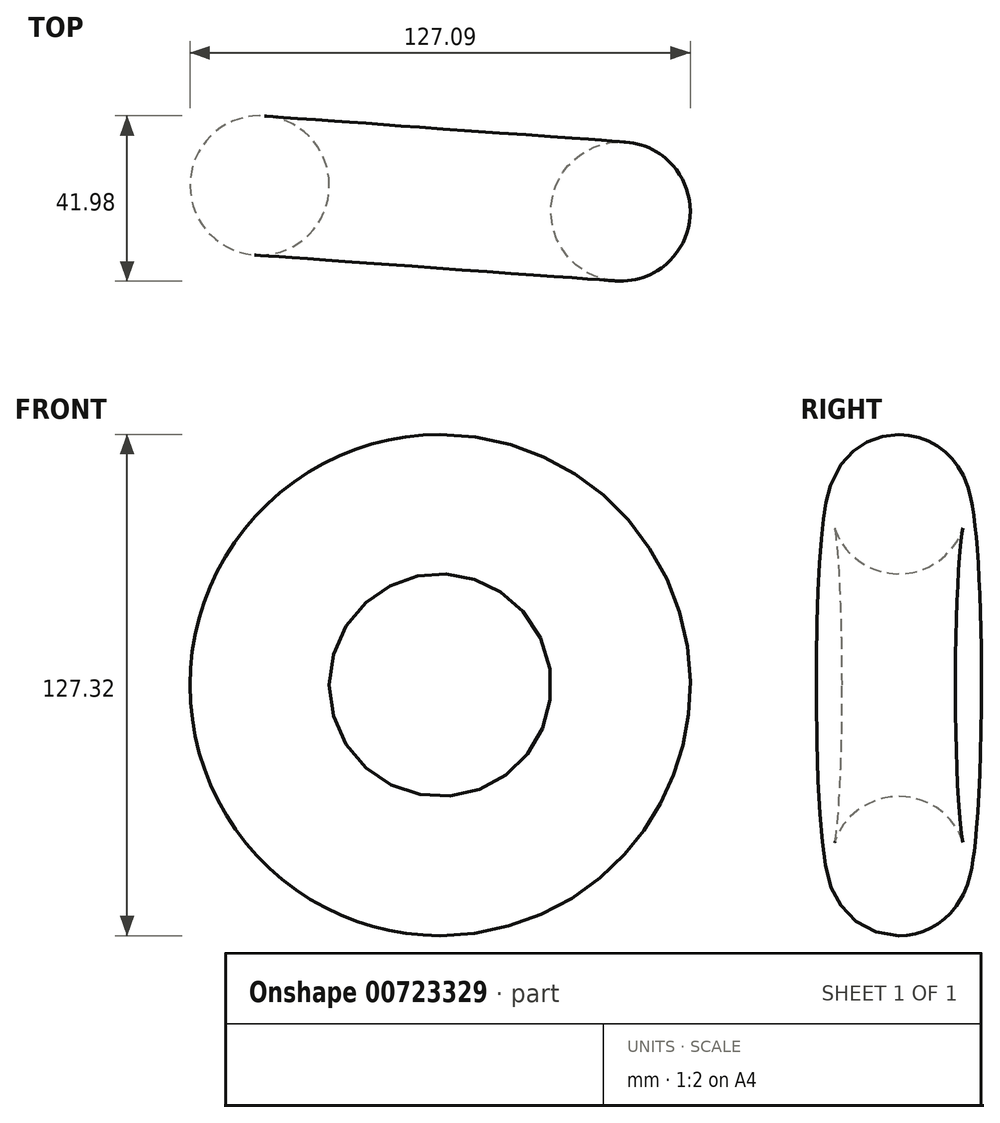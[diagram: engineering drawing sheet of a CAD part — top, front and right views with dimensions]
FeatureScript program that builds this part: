
annotation { "Feature Type Name" : "Feature", "Feature Type Description" : "" }
export const myFeature = defineFeature(function(context is Context, id is Id, definition is map)
    precondition{}
    {
        {
            var Q0;
            Q0=qCreatedBy(makeId("Top.planeOp"),FACE);
            var sketch = newSketch(context, id + "F0", { "sketchPlane" : qUnion([Q0])});
            skLineSegment(sketch, "E0", {"start": v(-14.74, 88.05) * mm, "end": v(-28.7, -105.89) * mm});
            skCircle(sketch, "E1", {"center": v(25.6, 8.15) * mm, "radius": 17.69 * mm});
            skSolve(sketch);
        }
        {
            var Q0;
            Q0 = qSketchRegion(id + "F0", true);
            var Q1;
            Q1=sQuery(id+"F0.wireOp",EDGE,"E0");
            revolve(context, id + "F1", {"surfaceOperationType" : NewSurfaceOperationType.NEW, "entities" : qUnion([Q0]), "axis" : qUnion([Q1]), "revolveType" : RevolveType.FULL});
        }
        {
            var Q0;
            Q0=qCreatedBy(makeId("Top.planeOp"),FACE);
            var sketch = newSketch(context, id + "F2", { "sketchPlane" : qUnion([Q0])});
            skFitSpline(sketch, "E2", {"points": [v(-39.88, 10.4) * mm, v(0, 149.84) * mm, v(-6.48, 199.8) * mm, v(-3.57, 226.94) * mm, v(0, 246.47) * mm, v(0, 302.77) * mm, v(0, 323.9) * mm, v(-6.22, 347) * mm, v(-11.34, 369.32) * mm], "startDerivative": vector(255.33, 909.75) * mm, "endDerivative": vector(125.62, 55.62) * mm});
            skSolve(sketch);
        }
        {
            var Q0;
            Q0=sQuery(id+"F2.wireOp",VERTEX,"E2.8.internal");
            var Q1;
            Q1=sQuery(id+"F2.wireOp",EDGE,"E2");
            cPlane(context, id + "F3", {"entities" : qUnion([Q0, Q1]), "cplaneType" : CPlaneType.CURVE_POINT, "offset" : 25 * mm, "width" : 150 * mm, "height" : 150 * mm});
        }
    });
